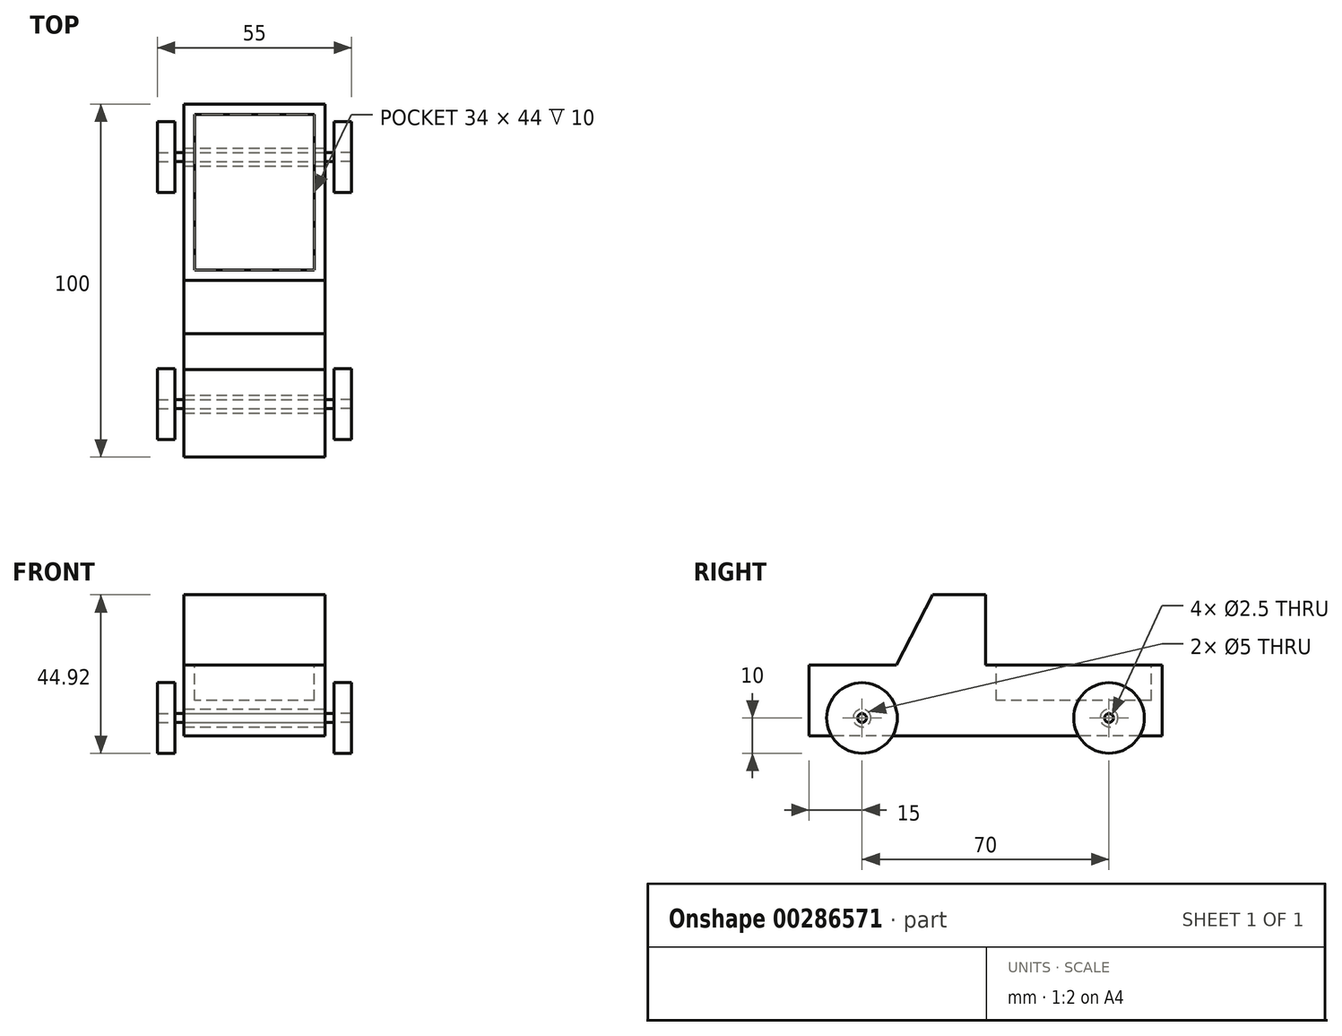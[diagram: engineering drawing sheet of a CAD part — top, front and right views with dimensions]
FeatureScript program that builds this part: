
annotation { "Feature Type Name" : "Feature", "Feature Type Description" : "" }
export const myFeature = defineFeature(function(context is Context, id is Id, definition is map)
    precondition{}
    {
        {
            var Q0;
            Q0=qCreatedBy(makeId("Right.planeOp"),FACE);
            var sketch = newSketch(context, id + "F0", { "sketchPlane" : qUnion([Q0])});
            skLineSegment(sketch, "E0.bottom", {"start": v(50, 10) * mm, "end": v(-50, 10) * mm});
            skLineSegment(sketch, "E0.top", {"start": v(50, -10) * mm, "end": v(-50, -10) * mm});
            skLineSegment(sketch, "E0.left", {"start": v(50, 10) * mm, "end": v(50, -10) * mm});
            skLineSegment(sketch, "E0.right", {"start": v(-50, 10) * mm, "end": v(-50, -10) * mm});
            skPoint(sketch, "E0.middle", {"position": v(0, 0) * mm});
            skSolve(sketch);
        }
        {
            var Q0;
            Q0=makeQuery(id+"F0.imprint","IMPRINT",FACE,{"disambiguationData":[TD([[makeQuery(id+"F0.imprint","IMPRINT",EDGE,{"derivedFrom":sQuery(id+"F0.wireOp",EDGE,"E0.bottom")}),1.0]])]});
            extrude(context, id + "F1", {"entities" : qUnion([Q0]), "depth" : 40 * mm});
        }
        {
            var Q0;
            Q0=makeQuery(id+"F1.opExtrude","CAP_FACE",FACE,{"disambiguationData":[OSD([sQuery(id+"F0.wireOp",EDGE,"E0.bottom"),sQuery(id+"F0.wireOp",EDGE,"E0.top"),sQuery(id+"F0.wireOp",EDGE,"E0.left"),sQuery(id+"F0.wireOp",EDGE,"E0.right")])],"isStart":false});
            var sketch = newSketch(context, id + "F2", { "sketchPlane" : qUnion([Q0])});
            skCircle(sketch, "E1", {"center": v(35, -5) * mm, "radius": 2.5 * mm});
            skSolve(sketch);
        }
        {
            var Q0;
            Q0=makeQuery(id+"F2.imprint","IMPRINT",FACE,{"disambiguationData":[TD([[makeQuery(id+"F2.imprint","IMPRINT",EDGE,{"derivedFrom":sQuery(id+"F2.wireOp",EDGE,"E1")}),1.0]])]});
            extrude(context, id + "F3", {"entities" : qUnion([Q0]), "operationType" : NewBodyOperationType.REMOVE, "endBound" : BoundingType.THROUGH_ALL, "oppositeDirection" : true, "depth" : 25 * mm});
        }
        {
            var Q0;
            Q0=makeQuery(id+"F1.opExtrude","CAP_FACE",FACE,{"disambiguationData":[OSD([sQuery(id+"F0.wireOp",EDGE,"E0.bottom"),sQuery(id+"F0.wireOp",EDGE,"E0.top"),sQuery(id+"F0.wireOp",EDGE,"E0.left"),sQuery(id+"F0.wireOp",EDGE,"E0.right")])],"isStart":false});
            var sketch = newSketch(context, id + "F4", { "sketchPlane" : qUnion([Q0])});
            skCircle(sketch, "E2", {"center": v(-35, -5) * mm, "radius": 2.5 * mm});
            skSolve(sketch);
        }
        {
            var Q0;
            Q0=makeQuery(id+"F4.imprint","IMPRINT",FACE,{"disambiguationData":[TD([[makeQuery(id+"F4.imprint","IMPRINT",EDGE,{"derivedFrom":sQuery(id+"F4.wireOp",EDGE,"E2")}),1.0]])]});
            extrude(context, id + "F5", {"entities" : qUnion([Q0]), "operationType" : NewBodyOperationType.REMOVE, "endBound" : BoundingType.THROUGH_ALL, "oppositeDirection" : true, "depth" : 25 * mm});
        }
        {
            var Q0;
            Q0=qCreatedBy(makeId("Right.planeOp"),FACE);
            var sketch = newSketch(context, id + "F6", { "sketchPlane" : qUnion([Q0])});
            skLineSegment(sketch, "E3", {"start": v(0, 9.92) * mm, "end": v(0, 29.92) * mm});
            skLineSegment(sketch, "E4", {"start": v(0, 29.92) * mm, "end": v(-15, 29.92) * mm});
            skLineSegment(sketch, "E5", {"start": v(-15, 29.92) * mm, "end": v(-25.3, 9.92) * mm});
            skLineSegment(sketch, "E6", {"start": v(0, 9.92) * mm, "end": v(-25.3, 9.92) * mm});
            skSolve(sketch);
        }
        {
            var Q0;
            Q0=makeQuery(id+"F6.imprint","IMPRINT",FACE,{"disambiguationData":[TD([[makeQuery(id+"F6.imprint","IMPRINT",EDGE,{"derivedFrom":sQuery(id+"F6.wireOp",EDGE,"E3")}),1.0]])]});
            extrude(context, id + "F7", {"entities" : qUnion([Q0]), "operationType" : NewBodyOperationType.ADD, "depth" : 40 * mm});
        }
        {
            var Q0;
            {var subQ0=sQuery(id+"F0.wireOp",EDGE,"E0.left");var subQ3=sQuery(id+"F0.wireOp",EDGE,"E0.bottom");Q0=makeQuery(id+"F7.boolean.opBoolean","SPLIT",FACE,{"disambiguationData":[TD([makeQuery(id+"F1.opExtrude","SWEPT_FACE",FACE,{"disambiguationData":[OSD([subQ0])]})])],"derivedFrom":makeQuery(id+"F1.opExtrude","SWEPT_FACE",FACE,{"disambiguationData":[OSD([subQ3])]})});}
            var sketch = newSketch(context, id + "F8", { "sketchPlane" : qUnion([Q0])});
            skLineSegment(sketch, "E7.0", {"start": v(3, 47) * mm, "end": v(3, 3) * mm});
            skLineSegment(sketch, "E7.1", {"start": v(37, 47) * mm, "end": v(3, 47) * mm});
            skLineSegment(sketch, "E7.2", {"start": v(37, 47) * mm, "end": v(37, 3) * mm});
            skLineSegment(sketch, "E7.3", {"start": v(37, 3) * mm, "end": v(3, 3) * mm});
            skSolve(sketch);
        }
        {
            var Q0;
            Q0=makeQuery(id+"F8.imprint","IMPRINT",FACE,{"disambiguationData":[TD([[makeQuery(id+"F8.imprint","IMPRINT",EDGE,{"derivedFrom":sQuery(id+"F8.wireOp",EDGE,"E7.0")}),1.0]])]});
            extrude(context, id + "F9", {"entities" : qUnion([Q0]), "operationType" : NewBodyOperationType.REMOVE, "oppositeDirection" : true, "depth" : 10 * mm});
        }
        {
            var Q0;
            Q0=makeQuery(id+"F7.boolean.opBoolean","MERGE",FACE,{"derivedFrom":[makeQuery(id+"F1.opExtrude","CAP_FACE",FACE,{"disambiguationData":[OSD([sQuery(id+"F0.wireOp",EDGE,"E0.bottom"),sQuery(id+"F0.wireOp",EDGE,"E0.top"),sQuery(id+"F0.wireOp",EDGE,"E0.left"),sQuery(id+"F0.wireOp",EDGE,"E0.right")])],"isStart":false}),makeQuery(id+"F7.opExtrude","CAP_FACE",FACE,{"disambiguationData":[OSD([sQuery(id+"F6.wireOp",EDGE,"E3"),sQuery(id+"F6.wireOp",EDGE,"E4"),sQuery(id+"F6.wireOp",EDGE,"E5"),sQuery(id+"F6.wireOp",EDGE,"E6")])],"isStart":false})]});
            var sketch = newSketch(context, id + "F10", { "sketchPlane" : qUnion([Q0])});
            skCircle(sketch, "E8", {"center": v(35, -5) * mm, "radius": 1.25 * mm});
            skCircle(sketch, "E9", {"center": v(-35, -5) * mm, "radius": 1.25 * mm});
            skSolve(sketch);
        }
        {
            var Q0;
            Q0=makeQuery(id+"F10.imprint","IMPRINT",FACE,{"disambiguationData":[TD([[makeQuery(id+"F10.imprint","IMPRINT",EDGE,{"derivedFrom":sQuery(id+"F10.wireOp",EDGE,"E8")}),1.0]])]});
            var Q1;
            Q1=sQuery(id+"F10.wireOp",EDGE,"E8");
            extrude(context, id + "F11", {"entities" : qUnion([Q0]), "surfaceEntities" : qUnion([Q1]), "oppositeDirection" : true, "depth" : 42.5 * mm});
        }
        {
            var Q0;
            Q0=makeQuery(id+"F11.opExtrude","CAP_FACE",FACE,{"disambiguationData":[OSD([sQuery(id+"F10.wireOp",EDGE,"E8")])],"isStart":true});
            var sketch = newSketch(context, id + "F12", { "sketchPlane" : qUnion([Q0])});
            skSolve(sketch);
        }
        {
            var Q0;
            Q0=makeQuery(id+"F12.imprint","IMPRINT",FACE,{"disambiguationData":[TD([[makeQuery(id+"F12.imprint","IMPRINT",EDGE,{"derivedFrom":makeQuery(id+"F11.opExtrude","CAP_EDGE",EDGE,{"disambiguationData":[OSD([sQuery(id+"F10.wireOp",EDGE,"E8")])],"isStart":true})}),1.0]])]});
            extrude(context, id + "F13", {"entities" : qUnion([Q0]), "operationType" : NewBodyOperationType.ADD, "depth" : 2.5 * mm});
        }
        {
            var Q0;
            Q0=makeQuery(id+"F7.boolean.opBoolean","MERGE",FACE,{"derivedFrom":[makeQuery(id+"F1.opExtrude","CAP_FACE",FACE,{"disambiguationData":[OSD([sQuery(id+"F0.wireOp",EDGE,"E0.bottom"),sQuery(id+"F0.wireOp",EDGE,"E0.top"),sQuery(id+"F0.wireOp",EDGE,"E0.left"),sQuery(id+"F0.wireOp",EDGE,"E0.right")])],"isStart":false}),makeQuery(id+"F7.opExtrude","CAP_FACE",FACE,{"disambiguationData":[OSD([sQuery(id+"F6.wireOp",EDGE,"E3"),sQuery(id+"F6.wireOp",EDGE,"E4"),sQuery(id+"F6.wireOp",EDGE,"E5"),sQuery(id+"F6.wireOp",EDGE,"E6")])],"isStart":false})]});
            var sketch = newSketch(context, id + "F14", { "sketchPlane" : qUnion([Q0])});
            skCircle(sketch, "E10", {"center": v(-35, -5) * mm, "radius": 1.25 * mm});
            skSolve(sketch);
        }
        {
            var Q0;
            Q0=makeQuery(id+"F14.imprint","IMPRINT",FACE,{"disambiguationData":[TD([[makeQuery(id+"F14.imprint","IMPRINT",EDGE,{"derivedFrom":sQuery(id+"F14.wireOp",EDGE,"E10")}),1.0]])]});
            extrude(context, id + "F15", {"entities" : qUnion([Q0]), "oppositeDirection" : true, "depth" : 42.5 * mm});
        }
        {
            var Q0;
            Q0=makeQuery(id+"F15.opExtrude","CAP_FACE",FACE,{"disambiguationData":[OSD([sQuery(id+"F14.wireOp",EDGE,"E10")])],"isStart":true});
            extrude(context, id + "F16", {"entities" : qUnion([Q0]), "operationType" : NewBodyOperationType.ADD, "depth" : 2.5 * mm});
        }
        {
            var Q0;
            Q0=makeQuery(id+"F16.opExtrude","CAP_FACE",FACE,{"disambiguationData":[OSD([sQuery(id+"F14.wireOp",EDGE,"E10")])],"isStart":false});
            var sketch = newSketch(context, id + "F17", { "sketchPlane" : qUnion([Q0])});
            skCircle(sketch, "E11", {"center": v(-35, -5) * mm, "radius": 10 * mm});
            skSolve(sketch);
        }
        {
            var Q0;
            Q0=makeQuery(id+"F17.imprint","IMPRINT",FACE,{"disambiguationData":[TD([[makeQuery(id+"F17.imprint","IMPRINT",EDGE,{"derivedFrom":sQuery(id+"F17.wireOp",EDGE,"E11")}),1.0]])]});
            extrude(context, id + "F18", {"entities" : qUnion([Q0]), "operationType" : NewBodyOperationType.ADD, "depth" : 5 * mm});
        }
        {
            var Q0;
            Q0=makeQuery(id+"F13.opExtrude","CAP_FACE",FACE,{"disambiguationData":[OSD([sQuery(id+"F10.wireOp",EDGE,"E8")])],"isStart":false});
            var sketch = newSketch(context, id + "F19", { "sketchPlane" : qUnion([Q0])});
            skCircle(sketch, "E12", {"center": v(35, -5) * mm, "radius": 10 * mm});
            skSolve(sketch);
        }
        {
            var Q0;
            Q0=makeQuery(id+"F19.imprint","IMPRINT",FACE,{"disambiguationData":[TD([[makeQuery(id+"F19.imprint","IMPRINT",EDGE,{"derivedFrom":sQuery(id+"F19.wireOp",EDGE,"E12")}),1.0]])]});
            extrude(context, id + "F20", {"entities" : qUnion([Q0]), "depth" : 5 * mm});
        }
        {
            var Q0;
            Q0=makeQuery(id+"F11.opExtrude","CAP_FACE",FACE,{"disambiguationData":[OSD([sQuery(id+"F10.wireOp",EDGE,"E8")])],"isStart":false});
            var sketch = newSketch(context, id + "F21", { "sketchPlane" : qUnion([Q0])});
            skCircle(sketch, "E13", {"center": v(-35, -5) * mm, "radius": 10 * mm});
            skSolve(sketch);
        }
        {
            var Q0;
            Q0=makeQuery(id+"F21.imprint","IMPRINT",FACE,{"disambiguationData":[TD([[makeQuery(id+"F21.imprint","IMPRINT",EDGE,{"derivedFrom":sQuery(id+"F21.wireOp",EDGE,"E13")}),1.0]])]});
            extrude(context, id + "F22", {"entities" : qUnion([Q0]), "depth" : 5 * mm});
        }
        {
            var Q0;
            Q0=makeQuery(id+"F15.opExtrude","CAP_FACE",FACE,{"disambiguationData":[OSD([sQuery(id+"F14.wireOp",EDGE,"E10")])],"isStart":false});
            var sketch = newSketch(context, id + "F23", { "sketchPlane" : qUnion([Q0])});
            skCircle(sketch, "E14", {"center": v(35, -5) * mm, "radius": 10 * mm});
            skSolve(sketch);
        }
        {
            var Q0;
            Q0=makeQuery(id+"F23.imprint","IMPRINT",FACE,{"disambiguationData":[TD([[makeQuery(id+"F23.imprint","IMPRINT",EDGE,{"derivedFrom":sQuery(id+"F23.wireOp",EDGE,"E14")}),1.0]])]});
            extrude(context, id + "F24", {"entities" : qUnion([Q0]), "depth" : 5 * mm});
        }
    });
